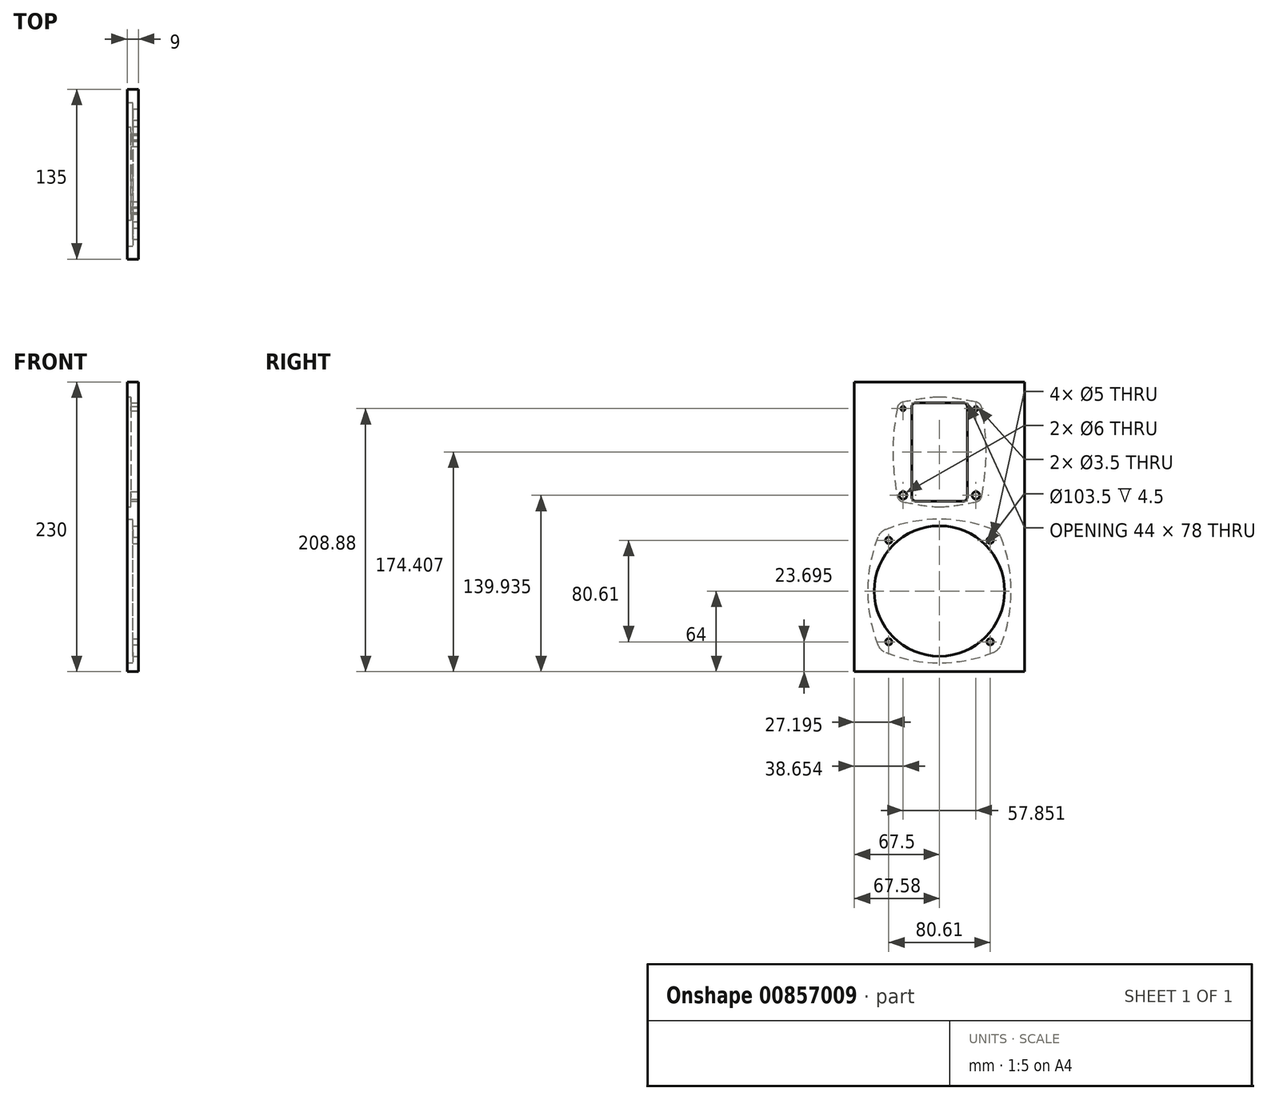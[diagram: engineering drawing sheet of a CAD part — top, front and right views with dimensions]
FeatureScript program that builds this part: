
annotation { "Feature Type Name" : "Feature", "Feature Type Description" : "" }
export const myFeature = defineFeature(function(context is Context, id is Id, definition is map)
    precondition{}
    {
        {
            var Q0;
            Q0=qCreatedBy(makeId("Right.planeOp"),FACE);
            var sketch = newSketch(context, id + "F0", { "sketchPlane" : qUnion([Q0])});
            skLineSegment(sketch, "E0.bottom", {"start": v(67.5, 115) * mm, "end": v(-67.5, 115) * mm});
            skLineSegment(sketch, "E0.left", {"start": v(67.5, 115) * mm, "end": v(67.5, -115) * mm});
            skLineSegment(sketch, "E0.right", {"start": v(-67.5, 115) * mm, "end": v(-67.5, -115) * mm});
            skLineSegment(sketch, "E1", {"start": v(67.5, -115) * mm, "end": v(-67.5, -115) * mm});
            skPoint(sketch, "E2", {"position": v(0, -51) * mm});
            skCircle(sketch, "E3", {"center": v(0, -51) * mm, "radius": 51.75 * mm});
            skCircle(sketch, "E4", {"center": v(40.3, -10.7) * mm, "radius": 2.5 * mm});
            skPoint(sketch, "E5", {"position": v(46.32, -4.68) * mm});
            skPoint(sketch, "E6", {"position": v(47.02, -3.98) * mm});
            skCircle(sketch, "E7.1.0", {"center": v(-40.3, -10.7) * mm, "radius": 2.5 * mm});
            skPoint(sketch, "E7.1.1", {"position": v(-46.32, -4.68) * mm});
            skPoint(sketch, "E7.1.2", {"position": v(-47.02, -3.98) * mm});
            skCircle(sketch, "E7.2.0", {"center": v(-40.3, -91.3) * mm, "radius": 2.5 * mm});
            skPoint(sketch, "E7.2.1", {"position": v(-46.32, -97.32) * mm});
            skPoint(sketch, "E7.2.2", {"position": v(-47.02, -98.02) * mm});
            skCircle(sketch, "E7.3.0", {"center": v(40.3, -91.3) * mm, "radius": 2.5 * mm});
            skPoint(sketch, "E7.3.1", {"position": v(46.32, -97.32) * mm});
            skPoint(sketch, "E7.3.2", {"position": v(47.02, -98.02) * mm});
            skPoint(sketch, "E8", {"position": v(1, 6) * mm});
            skPoint(sketch, "E9.1.0", {"position": v(-57, -51) * mm});
            skPoint(sketch, "E9.2.0", {"position": v(0, -108) * mm});
            skPoint(sketch, "E9.3.0", {"position": v(57, -51) * mm});
            skArc(sketch, "E10", {"start": v(47.02, -3.98) * mm, "mid": v(0, 6) * mm, "end": v(-47.02, -3.98) * mm});
            skArc(sketch, "E11", {"start": v(-47.02, -3.98) * mm, "mid": v(-57, -51) * mm, "end": v(-47.02, -98.02) * mm});
            skArc(sketch, "E12", {"start": v(-47.02, -98.02) * mm, "mid": v(0, -108) * mm, "end": v(47.02, -98.02) * mm});
            skArc(sketch, "E13", {"start": v(47.02, -98.02) * mm, "mid": v(57, -51) * mm, "end": v(47.02, -3.98) * mm});
            skLineSegment(sketch, "E14.trimOffspring", {"start": v(0, 6) * mm, "end": v(0, 115) * mm});
            skLineSegment(sketch, "E15.trimOffspring", {"start": v(46.32, -4.68) * mm, "end": v(47.02, -3.98) * mm});
            skPoint(sketch, "E16.start.orphan", {"position": v(0, -115) * mm});
            skLineSegment(sketch, "E17", {"start": v(0.08, 59.4) * mm, "end": v(0.08, 90.9) * mm});
            skLineSegment(sketch, "E18", {"start": v(0.08, 59.4) * mm, "end": v(0.08, 27.9) * mm});
            skLineSegment(sketch, "E19.bottom", {"start": v(0.08, 90.9) * mm, "end": v(0, 90.9) * mm});
            skLineSegment(sketch, "E19.top", {"start": v(0.08, 27.9) * mm, "end": v(0, 27.9) * mm});
            skPoint(sketch, "E20.visualSharp", {"position": v(16.58, 27.9) * mm});
            skArc(sketch, "E21", {"start": v(0.08, 90.9) * mm, "mid": v(0.04, 90.82) * mm, "end": v(0, 90.73) * mm});
            skArc(sketch, "E22", {"start": v(0, 28.08) * mm, "mid": v(0.04, 28) * mm, "end": v(0.08, 27.9) * mm});
            skPoint(sketch, "E23", {"position": v(0.08, 102.9) * mm});
            skPoint(sketch, "E24", {"position": v(0.08, 15.9) * mm});
            skPoint(sketch, "E25", {"position": v(-36.92, 59.4) * mm});
            skPoint(sketch, "E26", {"position": v(37.08, 59.4) * mm});
            skPoint(sketch, "E27", {"position": v(29, 93.88) * mm});
            skCircle(sketch, "E28", {"center": v(29, 93.88) * mm, "radius": 3 * mm});
            skCircle(sketch, "E29", {"center": v(-28.85, 93.88) * mm, "radius": 3 * mm});
            skLineSegment(sketch, "E30", {"start": v(0.08, 59.4) * mm, "end": v(0, 59.4) * mm});
            skLineSegment(sketch, "E31", {"start": v(0, 59.4) * mm, "end": v(0.08, 59.4) * mm});
            skPoint(sketch, "E32.MirrorP", {"position": v(29, 24.94) * mm});
            skCircle(sketch, "E33.MirrorC", {"center": v(-28.85, 24.94) * mm, "radius": 3 * mm});
            skCircle(sketch, "E34.MirrorC", {"center": v(29, 24.94) * mm, "radius": 3 * mm});
            skPoint(sketch, "E35", {"position": v(32.86, 98.48) * mm});
            skPoint(sketch, "E36.MirrorP", {"position": v(-32.7, 98.48) * mm});
            skPoint(sketch, "E37.MirrorP", {"position": v(32.86, 20.34) * mm});
            skPoint(sketch, "E38.MirrorP", {"position": v(-32.7, 20.34) * mm});
            skFitSpline(sketch, "E39", {"points": [v(32.86, 98.48) * mm, v(0.08, 102.9) * mm, v(-32.7, 98.48) * mm], "startDerivative": vector(-65.56, 9.7) * mm, "endDerivative": vector(-65.56, -9.7) * mm});
            skFitSpline(sketch, "E40", {"points": [v(-32.7, 98.48) * mm, v(-36.92, 59.4) * mm, v(-32.7, 20.34) * mm], "startDerivative": vector(-15.65, -78.14) * mm, "endDerivative": vector(15.65, -78.14) * mm});
            skFitSpline(sketch, "E41", {"points": [v(-32.7, 20.34) * mm, v(0.08, 15.9) * mm, v(32.86, 20.34) * mm], "startDerivative": vector(65.56, -9.7) * mm, "endDerivative": vector(65.56, 9.7) * mm});
            skFitSpline(sketch, "E42", {"points": [v(32.86, 20.34) * mm, v(37.08, 59.4) * mm, v(32.86, 98.48) * mm], "startDerivative": vector(15.65, 78.14) * mm, "endDerivative": vector(-15.65, 78.14) * mm});
            skCircle(sketch, "E43", {"center": v(29, 93.88) * mm, "radius": 1.75 * mm});
            skCircle(sketch, "E44", {"center": v(-28.85, 93.88) * mm, "radius": 1.75 * mm});
            skCircle(sketch, "E45", {"center": v(29, 24.94) * mm, "radius": 1.75 * mm});
            skCircle(sketch, "E46", {"center": v(-28.85, 24.94) * mm, "radius": 1.75 * mm});
            skPoint(sketch, "E47.orphan", {"position": v(0.08, 59.4) * mm});
            skLineSegment(sketch, "E48.bottom", {"start": v(19.08, 98.4) * mm, "end": v(-18.92, 98.4) * mm});
            skLineSegment(sketch, "E48.top", {"start": v(19.08, 20.4) * mm, "end": v(-18.92, 20.4) * mm});
            skLineSegment(sketch, "E48.left", {"start": v(22.08, 95.4) * mm, "end": v(22.08, 23.4) * mm});
            skLineSegment(sketch, "E48.right", {"start": v(-21.92, 95.4) * mm, "end": v(-21.92, 23.4) * mm});
            skPoint(sketch, "E49.visualSharp", {"position": v(22.08, 98.4) * mm});
            skArc(sketch, "E49.filletArc", {"start": v(22.08, 95.4) * mm, "mid": v(21.2, 97.53) * mm, "end": v(19.08, 98.4) * mm});
            skPoint(sketch, "E50.visualSharp", {"position": v(-21.92, 98.4) * mm});
            skArc(sketch, "E50.filletArc", {"start": v(-18.92, 98.4) * mm, "mid": v(-21.04, 97.53) * mm, "end": v(-21.92, 95.4) * mm});
            skPoint(sketch, "E51.visualSharp", {"position": v(-21.92, 20.4) * mm});
            skArc(sketch, "E51.filletArc", {"start": v(-21.92, 23.4) * mm, "mid": v(-21.04, 21.29) * mm, "end": v(-18.92, 20.4) * mm});
            skPoint(sketch, "E52.visualSharp", {"position": v(22.08, 20.4) * mm});
            skArc(sketch, "E52.filletArc", {"start": v(19.08, 20.4) * mm, "mid": v(21.2, 21.29) * mm, "end": v(22.08, 23.4) * mm});
            skSolve(sketch);
        }
        {
            var Q0;
            {var subQ4=sQuery(id+"F0.wireOp",EDGE,"E0.left");Q0=makeQuery(id+"F0.imprint","IMPRINT",FACE,{"disambiguationData":[TD([[makeQuery(id+"F0.imprint","IMPRINT",EDGE,{"derivedFrom":subQ4}),-1.0]])]});}
            extrude(context, id + "F1", {"entities" : qUnion([Q0]), "oppositeDirection" : true, "depth" : 9 * mm, "offsetDistance" : 25 * mm});
        }
        {
            var Q0;
            Q0=makeQuery(id+"F0.imprint","IMPRINT",FACE,{"disambiguationData":[TD([[makeQuery(id+"F0.imprint","IMPRINT",EDGE,{"derivedFrom":sQuery(id+"F0.wireOp",EDGE,"E3")}),-1.0]])]});
            extrude(context, id + "F2", {"entities" : qUnion([Q0]), "operationType" : NewBodyOperationType.ADD, "oppositeDirection" : true, "depth" : 4.5 * mm, "offsetDistance" : 25 * mm});
        }
        {
            var Q0;
            Q0=makeQuery(id+"F1.opExtrude","SWEPT_EDGE",EDGE,{"disambiguationData":[OSD([sQuery(id+"F0.wireOp",EDGE,"ZpgzB6W4-esGr-Y8vB-Hv0B-G3QVkJXGVfF8"),sQuery(id+"F0.wireOp",EDGE,"E10"),sQuery(id+"F0.wireOp",EDGE,"E13")])]});
            var Q1;
            Q1=makeQuery(id+"F1.opExtrude","SWEPT_EDGE",EDGE,{"disambiguationData":[OSD([sQuery(id+"F0.wireOp",EDGE,"E10"),sQuery(id+"F0.wireOp",EDGE,"E11")])]});
            var Q2;
            Q2=makeQuery(id+"F1.opExtrude","SWEPT_EDGE",EDGE,{"disambiguationData":[OSD([sQuery(id+"F0.wireOp",EDGE,"E11"),sQuery(id+"F0.wireOp",EDGE,"E12")])]});
            var Q3;
            Q3=makeQuery(id+"F1.opExtrude","SWEPT_EDGE",EDGE,{"disambiguationData":[OSD([sQuery(id+"F0.wireOp",EDGE,"E12"),sQuery(id+"F0.wireOp",EDGE,"E13")])]});
            fillet(context, id + "F3", {"entities" : qUnion([Q0, Q1, Q2, Q3]), "radius" : 11 * mm, "tangentPropagation" : true, "allowEdgeOverflow" : false});
        }
        {
            var Q0;
            Q0=makeQuery(id+"F0.imprint","IMPRINT",FACE,{"disambiguationData":[TD([[makeQuery(id+"F0.imprint","IMPRINT",EDGE,{"derivedFrom":sQuery(id+"F0.wireOp",EDGE,"E19.left")}),1.0]])]});
            var Q1;
            Q1=makeQuery(id+"F0.imprint","IMPRINT",FACE,{"disambiguationData":[TD([[makeQuery(id+"F0.imprint","IMPRINT",EDGE,{"derivedFrom":sQuery(id+"F0.wireOp",EDGE,"E19.right")}),-1.0]])]});
            var Q2;
            Q2=makeQuery(id+"F0.imprint","IMPRINT",FACE,{"disambiguationData":[TD([[makeQuery(id+"F0.imprint","IMPRINT",EDGE,{"derivedFrom":sQuery(id+"F0.wireOp",EDGE,"E28")}),-1.0]])]});
            var Q3;
            Q3=makeQuery(id+"F0.imprint","IMPRINT",FACE,{"disambiguationData":[TD([[makeQuery(id+"F0.imprint","IMPRINT",EDGE,{"derivedFrom":sQuery(id+"F0.wireOp",EDGE,"E29")}),-1.0]])]});
            var Q4;
            Q4=makeQuery(id+"F0.imprint","IMPRINT",FACE,{"disambiguationData":[TD([[makeQuery(id+"F0.imprint","IMPRINT",EDGE,{"derivedFrom":sQuery(id+"F0.wireOp",EDGE,"E28")}),1.0]])]});
            var Q5;
            Q5=makeQuery(id+"F0.imprint","IMPRINT",FACE,{"disambiguationData":[TD([[makeQuery(id+"F0.imprint","IMPRINT",EDGE,{"derivedFrom":sQuery(id+"F0.wireOp",EDGE,"E34.MirrorC")}),-1.0]])]});
            var Q6;
            Q6=makeQuery(id+"F0.imprint","IMPRINT",FACE,{"disambiguationData":[TD([[makeQuery(id+"F0.imprint","IMPRINT",EDGE,{"derivedFrom":sQuery(id+"F0.wireOp",EDGE,"E33.MirrorC")}),-1.0]])]});
            var Q7;
            Q7=makeQuery(id+"F0.imprint","IMPRINT",FACE,{"disambiguationData":[TD([[makeQuery(id+"F0.imprint","IMPRINT",EDGE,{"derivedFrom":sQuery(id+"F0.wireOp",EDGE,"E29")}),1.0]])]});
            extrude(context, id + "F4", {"entities" : qUnion([Q0, Q1, Q2, Q3, Q4, Q5, Q6, Q7]), "operationType" : NewBodyOperationType.ADD, "oppositeDirection" : true, "depth" : 6 * mm, "offsetDistance" : 25 * mm});
        }
        {
            var Q0;
            Q0=makeQuery(id+"F1.opExtrude","SWEPT_EDGE",EDGE,{"disambiguationData":[OSD([sQuery(id+"F0.wireOp",EDGE,"E39"),sQuery(id+"F0.wireOp",EDGE,"E42")])]});
            var Q1;
            Q1=makeQuery(id+"F1.opExtrude","SWEPT_EDGE",EDGE,{"disambiguationData":[OSD([sQuery(id+"F0.wireOp",EDGE,"E41"),sQuery(id+"F0.wireOp",EDGE,"E42")])]});
            var Q2;
            Q2=makeQuery(id+"F1.opExtrude","SWEPT_EDGE",EDGE,{"disambiguationData":[OSD([sQuery(id+"F0.wireOp",EDGE,"E40"),sQuery(id+"F0.wireOp",EDGE,"E41")])]});
            var Q3;
            Q3=makeQuery(id+"F1.opExtrude","SWEPT_EDGE",EDGE,{"disambiguationData":[OSD([sQuery(id+"F0.wireOp",EDGE,"E39"),sQuery(id+"F0.wireOp",EDGE,"E40")])]});
            fillet(context, id + "F5", {"entities" : qUnion([Q0, Q1, Q2, Q3]), "radius" : 6 * mm, "tangentPropagation" : true, "allowEdgeOverflow" : false});
        }
    });
